# Revit family: Sanitary_Toilets_hansgrohe_22468CHN-MitaPura-Original-S-WC-Seat-Cover_SoftClose_QuickRelease
name_source: partatom
category: Plumbing Fixtures
units: mm (PartAtom-declared; Revit-internal decimal feet)

## family parameters
Cut with Voids When Loaded = Yes
Host = Face
Maintain Annotation Orientation = No
OmniClass Number = 23.31.19.19.17
OmniClass Title = Water Closet Seats
Part Type = Normal
Room Calculation Point = No
Round Connector Dimension = Use Diameter
Shared = No

## types (1)
- 007 White
    Default Elevation = 0 mm  [stored 0 ft]
    Description = MitaPura Original S WC seat and cover elongated with SoftClose and QuickRelease
    Manufacturer = Hansgrohe
    Material 1 = Hansgrohe - Plastic - White
    Model = 22468CHN
    Product Page URL = https://www.hansgrohe.com
    Product data url = https://bimobject.com
    URL = https://www.hansgrohe.com
    Version = 1

note: [stored X ft] marks values corroborated as IEEE doubles in the binary element streams (Revit-internal decimal feet)

## geometry (parser evidence)
native form markers: Sweep x5
no freeform markers — native parametric forms only
